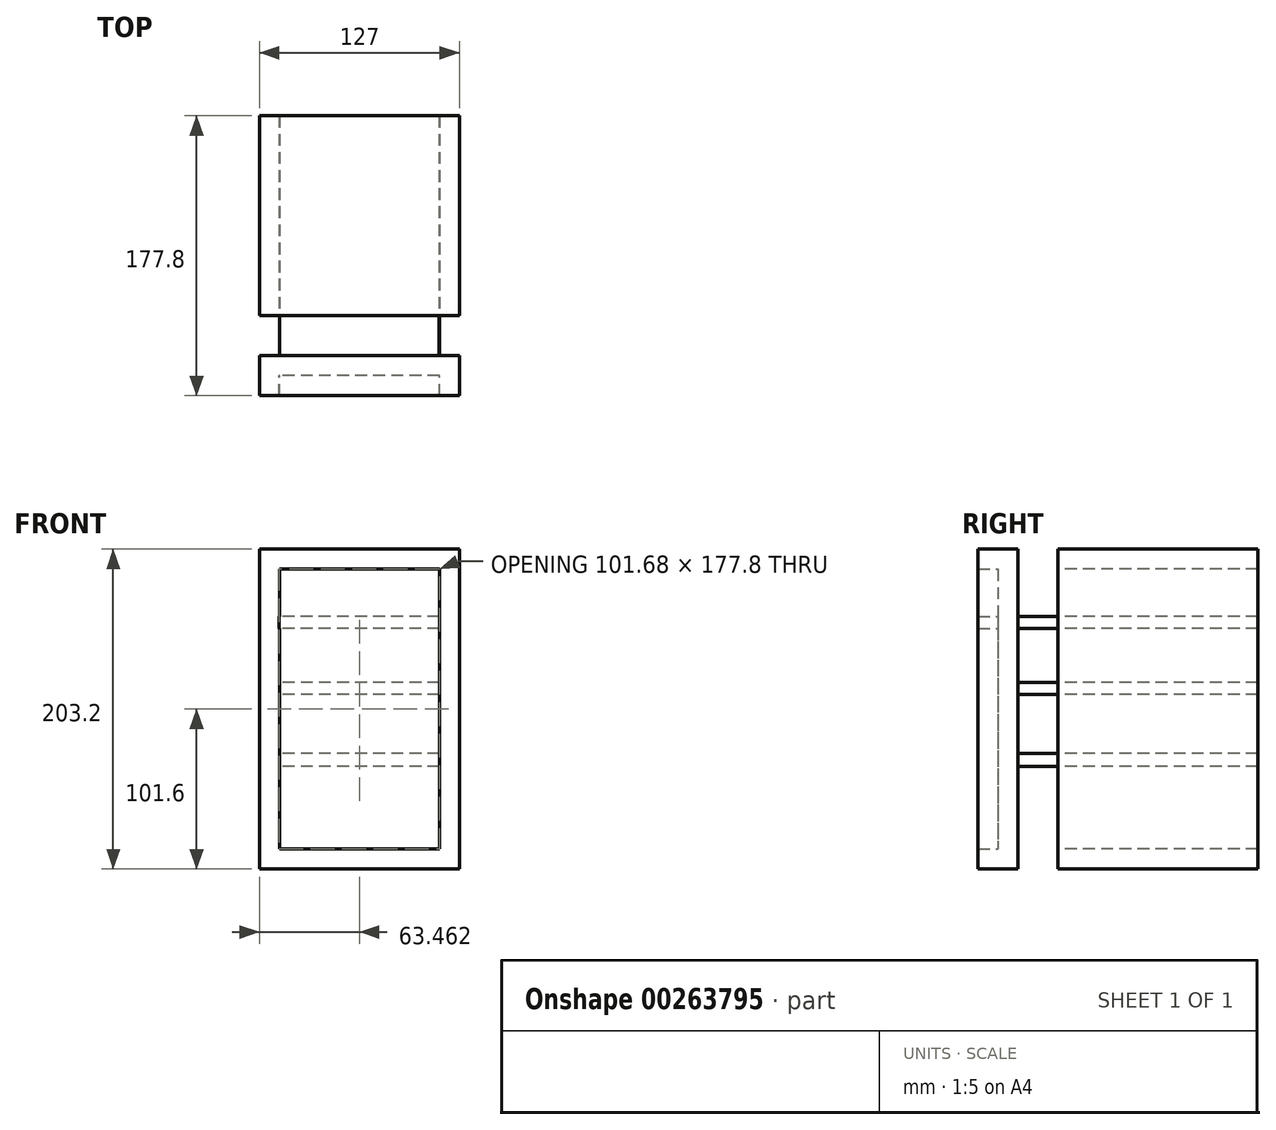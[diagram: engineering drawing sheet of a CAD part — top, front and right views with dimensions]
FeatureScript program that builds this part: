
annotation { "Feature Type Name" : "Feature", "Feature Type Description" : "" }
export const myFeature = defineFeature(function(context is Context, id is Id, definition is map)
    precondition{}
    {
        {
            var Q0;
            Q0=qCreatedBy(makeId("Front.planeOp"),FACE);
            var sketch = newSketch(context, id + "F0", { "sketchPlane" : qUnion([Q0])});
            skPoint(sketch, "E0.middle", {"position": v(0, 0) * mm});
            skLineSegment(sketch, "E1.bottom", {"start": v(63.5, 101.6) * mm, "end": v(-63.5, 101.6) * mm});
            skLineSegment(sketch, "E1.top", {"start": v(63.5, -101.6) * mm, "end": v(-63.5, -101.6) * mm});
            skLineSegment(sketch, "E1.left", {"start": v(63.5, 101.6) * mm, "end": v(63.5, -101.6) * mm});
            skLineSegment(sketch, "E1.right", {"start": v(-63.5, 101.6) * mm, "end": v(-63.5, -101.6) * mm});
            skLineSegment(sketch, "E2.bottom", {"start": v(50.8, 88.9) * mm, "end": v(-50.8, 88.9) * mm});
            skLineSegment(sketch, "E2.top", {"start": v(50.8, -88.9) * mm, "end": v(-50.8, -88.9) * mm});
            skLineSegment(sketch, "E2.left", {"start": v(50.8, 88.9) * mm, "end": v(50.8, -88.9) * mm});
            skLineSegment(sketch, "E2.right", {"start": v(-50.8, 88.9) * mm, "end": v(-50.8, -88.9) * mm});
            skLineSegment(sketch, "E3.bottom", {"start": v(50.72, 58.91) * mm, "end": v(-50.88, 58.91) * mm});
            skLineSegment(sketch, "E3.top", {"start": v(50.72, 51.3) * mm, "end": v(-50.88, 51.3) * mm});
            skLineSegment(sketch, "E3.left", {"start": v(50.72, 58.91) * mm, "end": v(50.72, 51.3) * mm});
            skLineSegment(sketch, "E3.right", {"start": v(-50.88, 58.91) * mm, "end": v(-50.88, 51.3) * mm});
            skLineSegment(sketch, "E4.bottom", {"start": v(50.8, 9.22) * mm, "end": v(-50.8, 9.22) * mm});
            skLineSegment(sketch, "E4.top", {"start": v(50.8, 17.07) * mm, "end": v(-50.8, 17.07) * mm});
            skLineSegment(sketch, "E4.left", {"start": v(50.8, 9.22) * mm, "end": v(50.8, 17.07) * mm});
            skLineSegment(sketch, "E4.right", {"start": v(-50.8, 9.22) * mm, "end": v(-50.8, 17.07) * mm});
            skLineSegment(sketch, "E5.bottom", {"start": v(50.8, -28.14) * mm, "end": v(-50.8, -28.14) * mm});
            skLineSegment(sketch, "E5.top", {"start": v(50.8, -36.3) * mm, "end": v(-50.8, -36.3) * mm});
            skLineSegment(sketch, "E5.left", {"start": v(50.8, -28.14) * mm, "end": v(50.8, -36.3) * mm});
            skLineSegment(sketch, "E5.right", {"start": v(-50.8, -28.14) * mm, "end": v(-50.8, -36.3) * mm});
            skSolve(sketch);
        }
        {
            var Q0;
            Q0=makeQuery(id+"F0.imprint","IMPRINT",FACE,{"disambiguationData":[TD([[makeQuery(id+"F0.imprint","IMPRINT",EDGE,{"derivedFrom":sQuery(id+"F0.wireOp",EDGE,"E1.bottom")}),1.0]])]});
            extrude(context, id + "F1", {"entities" : qUnion([Q0]), "oppositeDirection" : true, "depth" : 152.4 * mm});
        }
        {
            var Q0;
            Q0=qCreatedBy(makeId("Front.planeOp"),FACE);
            var sketch = newSketch(context, id + "F2", { "sketchPlane" : qUnion([Q0])});
            skLineSegment(sketch, "E6.bottom", {"start": v(-63.5, 101.6) * mm, "end": v(63.5, 101.6) * mm});
            skLineSegment(sketch, "E6.top", {"start": v(-63.5, -101.6) * mm, "end": v(63.5, -101.6) * mm});
            skLineSegment(sketch, "E6.left", {"start": v(-63.5, 101.6) * mm, "end": v(-63.5, -101.6) * mm});
            skLineSegment(sketch, "E6.right", {"start": v(63.5, 101.6) * mm, "end": v(63.5, -101.6) * mm});
            skPoint(sketch, "E6.middle", {"position": v(0, 0) * mm});
            skSolve(sketch);
        }
        {
            var Q0;
            Q0=makeQuery(id+"F2.imprint","IMPRINT",FACE,{"disambiguationData":[TD([[makeQuery(id+"F2.imprint","IMPRINT",EDGE,{"derivedFrom":sQuery(id+"F2.wireOp",EDGE,"E6.bottom")}),-1.0]])]});
            extrude(context, id + "F3", {"entities" : qUnion([Q0]), "operationType" : NewBodyOperationType.REMOVE, "oppositeDirection" : true, "depth" : 25.4 * mm});
        }
        {
            var Q0;
            Q0 = qSketchRegion(id + "F0", true);
            extrude(context, id + "F4", {"entities" : qUnion([Q0]), "depth" : 25.4 * mm});
        }
        {
            var Q0;
            Q0 = qSketchRegion(id + "F0", true);
            extrude(context, id + "F5", {"entities" : qUnion([Q0]), "depth" : 25.4 * mm});
        }
        {
            var Q0;
            {var subQ5=sQuery(id+"F0.wireOp",EDGE,"E3.left");Q0=makeQuery(id+"F0.imprint","IMPRINT",FACE,{"disambiguationData":[TD([[makeQuery(id+"F0.imprint","IMPRINT",EDGE,{"derivedFrom":subQ5}),-1.0]])]});}
            extrude(context, id + "F6", {"entities" : qUnion([Q0]), "operationType" : NewBodyOperationType.ADD, "oppositeDirection" : true, "depth" : 152.4 * mm});
        }
        {
            var Q0;
            Q0=makeQuery(id+"F0.imprint","IMPRINT",FACE,{"disambiguationData":[TD([[makeQuery(id+"F0.imprint","IMPRINT",EDGE,{"derivedFrom":sQuery(id+"F0.wireOp",EDGE,"E4.bottom")}),-1.0]])]});
            extrude(context, id + "F7", {"entities" : qUnion([Q0]), "oppositeDirection" : true, "depth" : 152.4 * mm});
        }
        {
            var Q0;
            Q0=makeQuery(id+"F0.imprint","IMPRINT",FACE,{"disambiguationData":[TD([[makeQuery(id+"F0.imprint","IMPRINT",EDGE,{"derivedFrom":sQuery(id+"F0.wireOp",EDGE,"E5.bottom")}),1.0]])]});
            extrude(context, id + "F8", {"entities" : qUnion([Q0]), "oppositeDirection" : true, "depth" : 152.4 * mm});
        }
        {
            var Q0;
            Q0=qCreatedBy(makeId("Front.planeOp"),FACE);
            var sketch = newSketch(context, id + "F9", { "sketchPlane" : qUnion([Q0])});
            skLineSegment(sketch, "E7.bottom", {"start": v(63.5, 101.6) * mm, "end": v(-63.5, 101.6) * mm});
            skLineSegment(sketch, "E7.top", {"start": v(63.5, -101.6) * mm, "end": v(-63.5, -101.6) * mm});
            skLineSegment(sketch, "E7.left", {"start": v(63.5, 101.6) * mm, "end": v(63.5, -101.6) * mm});
            skLineSegment(sketch, "E7.right", {"start": v(-63.5, 101.6) * mm, "end": v(-63.5, -101.6) * mm});
            skPoint(sketch, "E7.middle", {"position": v(0, 0) * mm});
            skSolve(sketch);
        }
        {
            var Q0;
            Q0=makeQuery(id+"F9.imprint","IMPRINT",FACE,{"disambiguationData":[TD([[makeQuery(id+"F9.imprint","IMPRINT",EDGE,{"derivedFrom":sQuery(id+"F9.wireOp",EDGE,"E7.bottom")}),1.0]])]});
            extrude(context, id + "F10", {"entities" : qUnion([Q0]), "depth" : 12.7 * mm});
        }
        {
            var Q0;
            Q0=qCreatedBy(makeId("Front.planeOp"),FACE);
            var sketch = newSketch(context, id + "F11", { "sketchPlane" : qUnion([Q0])});
            skLineSegment(sketch, "E8.bottom", {"start": v(63.5, 101.6) * mm, "end": v(-63.5, 101.6) * mm});
            skLineSegment(sketch, "E8.top", {"start": v(63.5, -101.6) * mm, "end": v(-63.5, -101.6) * mm});
            skLineSegment(sketch, "E8.left", {"start": v(63.5, 101.6) * mm, "end": v(63.5, -101.6) * mm});
            skLineSegment(sketch, "E8.right", {"start": v(-63.5, 101.6) * mm, "end": v(-63.5, -101.6) * mm});
            skPoint(sketch, "E8.middle", {"position": v(0, 0) * mm});
            skLineSegment(sketch, "E9.bottom", {"start": v(-57.13, -22.53) * mm, "end": v(-52.6, -22.53) * mm});
            skLineSegment(sketch, "E9.top", {"start": v(-57.13, 57.04) * mm, "end": v(-52.6, 57.04) * mm});
            skLineSegment(sketch, "E9.left", {"start": v(-57.13, -22.53) * mm, "end": v(-57.13, 57.04) * mm});
            skLineSegment(sketch, "E9.right", {"start": v(-52.6, -22.53) * mm, "end": v(-52.6, 57.04) * mm});
            skSolve(sketch);
        }
        {
            var Q0;
            Q0=makeQuery(id+"F11.imprint","IMPRINT",FACE,{"disambiguationData":[TD([[makeQuery(id+"F11.imprint","IMPRINT",EDGE,{"derivedFrom":sQuery(id+"F11.wireOp",EDGE,"E9.bottom")}),1.0]])]});
            extrude(context, id + "F12", {"entities" : qUnion([Q0]), "depth" : 18.03 * mm});
        }
        {
            var Q0;
            Q0 = qSketchRegion(id + "F11", true);
            extrude(context, id + "F13", {"entities" : qUnion([Q0]), "operationType" : NewBodyOperationType.ADD, "depth" : 5.08 * mm});
        }
    });
